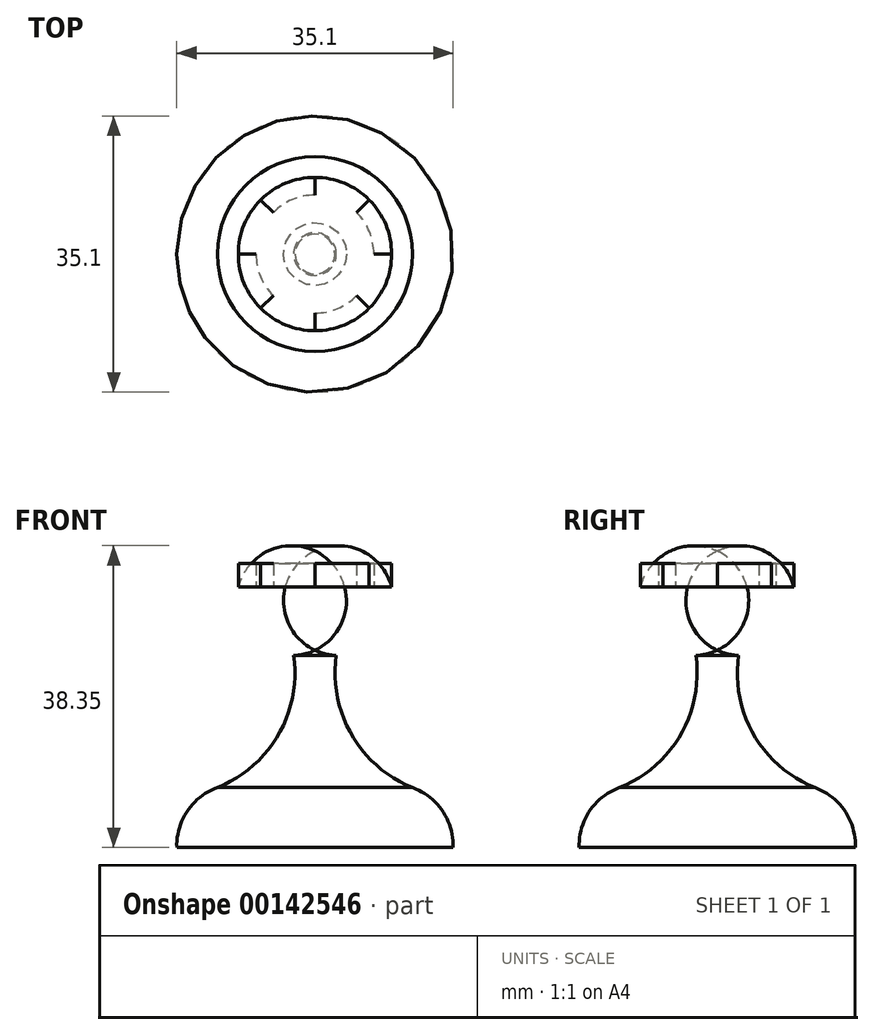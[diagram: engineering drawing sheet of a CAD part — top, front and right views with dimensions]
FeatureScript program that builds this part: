
annotation { "Feature Type Name" : "Feature", "Feature Type Description" : "" }
export const myFeature = defineFeature(function(context is Context, id is Id, definition is map)
    precondition{}
    {
        {
            var Q0;
            Q0=qCreatedBy(makeId("Front.planeOp"),FACE);
            var sketch = newSketch(context, id + "F0", { "sketchPlane" : qUnion([Q0])});
            skArc(sketch, "E0", {"start": v(17.54, 0) * mm, "mid": v(16.21, 4.65) * mm, "end": v(12.4, 7.62) * mm});
            skArc(sketch, "E1", {"start": v(2.7, 24.4) * mm, "mid": v(4.65, 14.33) * mm, "end": v(12.4, 7.62) * mm});
            skArc(sketch, "E2", {"start": v(2.7, 24.4) * mm, "mid": v(8.4, 26.98) * mm, "end": v(9.74, 33.08) * mm});
            skArc(sketch, "E3.MirrorCS", {"start": v(-2.7, 24.4) * mm, "mid": v(-8.4, 26.98) * mm, "end": v(-9.74, 33.08) * mm});
            skArc(sketch, "E4.MirrorCS", {"start": v(-2.7, 24.4) * mm, "mid": v(-4.65, 14.33) * mm, "end": v(-12.4, 7.62) * mm});
            skArc(sketch, "E5.MirrorCS", {"start": v(-17.54, 0) * mm, "mid": v(-16.21, 4.65) * mm, "end": v(-12.4, 7.62) * mm});
            skLineSegment(sketch, "E6", {"start": v(17.54, 0) * mm, "end": v(-17.54, 0) * mm});
            skLineSegment(sketch, "E7", {"start": v(9.74, 33.08) * mm, "end": v(-9.74, 33.08) * mm});
            skLineSegment(sketch, "E8", {"start": v(0, 0) * mm, "end": v(0, 33.08) * mm});
            skSolve(sketch);
        }
        {
            var Q0;
            {var subQ1=sQuery(id+"F0.wireOp",EDGE,"E0");Q0=makeQuery(id+"F0.imprint","IMPRINT",FACE,{"disambiguationData":[TD([[makeQuery(id+"F0.imprint","IMPRINT",EDGE,{"derivedFrom":subQ1}),1.0]])]});}
            var Q1;
            Q1=sQuery(id+"F0.wireOp",EDGE,"E8");
            revolve(context, id + "F1", {"entities" : qUnion([Q0]), "axis" : qUnion([Q1]), "revolveType" : RevolveType.FULL});
        }
        {
            var Q0;
            Q0=makeQuery(id+"F1.opRevolve","SWEPT_FACE",FACE,{"disambiguationData":[OSD([sQuery(id+"F0.wireOp",EDGE,"E7")])]});
            var sketch = newSketch(context, id + "F2", { "sketchPlane" : qUnion([Q0])});
            skArc(sketch, "E9", {"start": v(0, 9.74) * mm, "mid": v(-3.73, 9) * mm, "end": v(-6.89, 6.89) * mm});
            skArc(sketch, "E10", {"start": v(0, 7.49) * mm, "mid": v(-2.87, 6.92) * mm, "end": v(-5.3, 5.3) * mm});
            skLineSegment(sketch, "E11", {"start": v(-5.3, 5.3) * mm, "end": v(-6.89, 6.89) * mm});
            skLineSegment(sketch, "E12", {"start": v(0, 7.49) * mm, "end": v(0, 9.74) * mm});
            skSolve(sketch);
        }
        {
            var Q0;
            Q0=makeQuery(id+"F2.imprint","IMPRINT",FACE,{"disambiguationData":[TD([[makeQuery(id+"F2.imprint","IMPRINT",EDGE,{"derivedFrom":sQuery(id+"F2.wireOp",EDGE,"E9")}),-1.0]])]});
            extrude(context, id + "F3", {"entities" : qUnion([Q0]), "depth" : 3 * mm});
        }
        {
            var Q0;
            Q0=makeQuery(id+"F3.opExtrude","SWEPT_BODY",BODY,{"disambiguationData":[OSD([sQuery(id+"F2.wireOp",EDGE,"E9"),sQuery(id+"F2.wireOp",EDGE,"E10"),sQuery(id+"F2.wireOp",EDGE,"E11"),sQuery(id+"F2.wireOp",EDGE,"E12")])]});
            var Q1;
            Q1=makeQuery(id+"F1.opRevolve","SWEPT_EDGE",EDGE,{"disambiguationData":[OSD([sQuery(id+"F0.wireOp",EDGE,"E2"),sQuery(id+"F0.wireOp",EDGE,"E7")])]});
            circularPattern(context, id + "F4", {"entities" : qUnion([Q0]), "axis" : qUnion([Q1]), "angle" : 360 * degree, "instanceCount" : 4, "equalSpace" : true});
        }
    });
